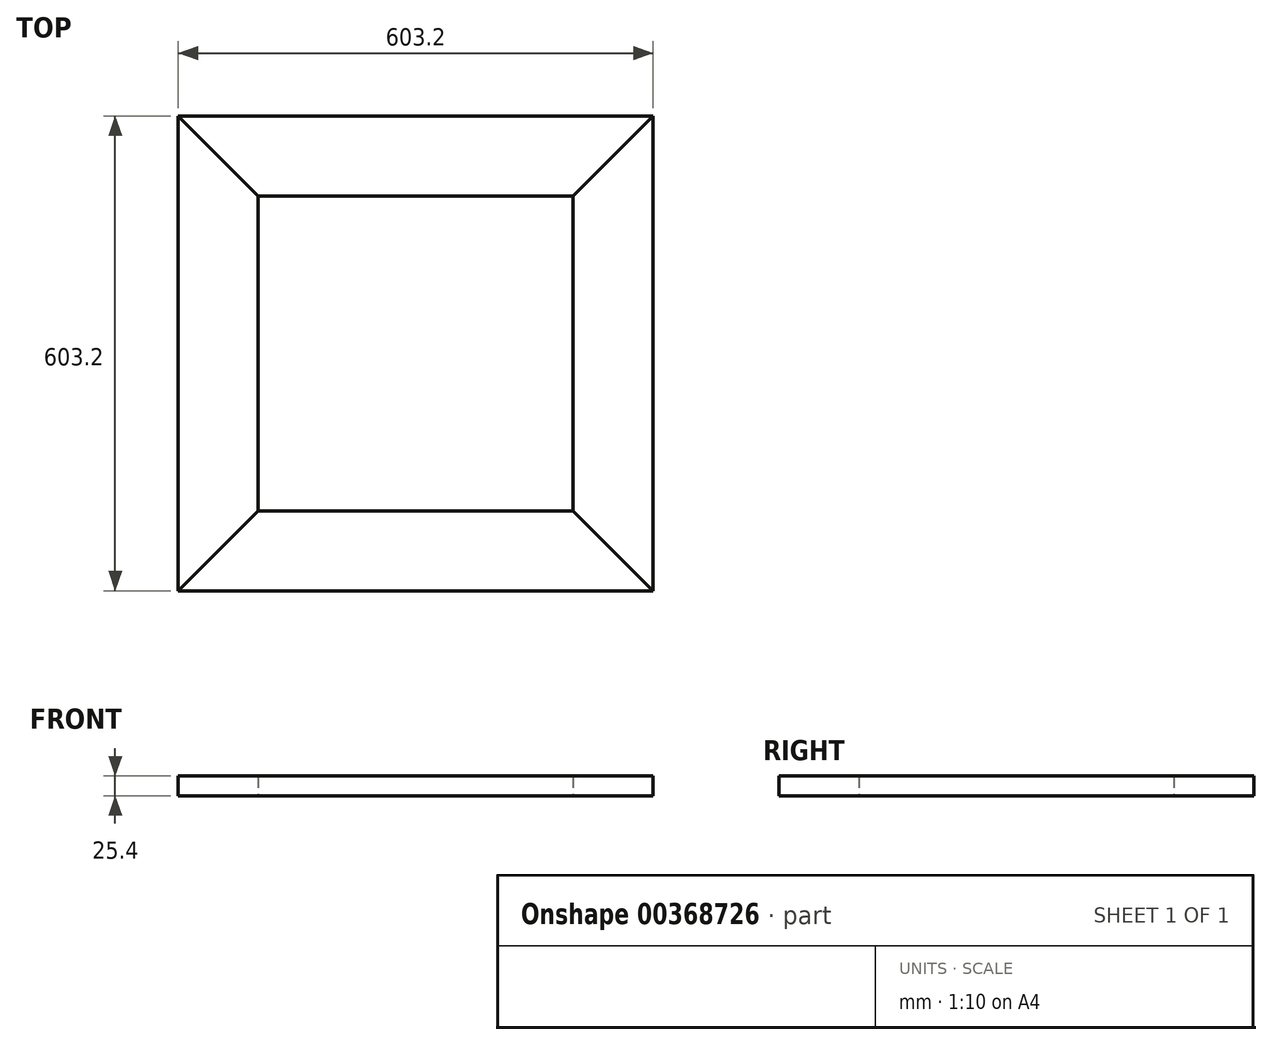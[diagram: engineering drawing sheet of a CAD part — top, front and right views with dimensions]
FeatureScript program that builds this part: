
annotation { "Feature Type Name" : "Feature", "Feature Type Description" : "" }
export const myFeature = defineFeature(function(context is Context, id is Id, definition is map)
    precondition{}
    {
        {
            var Q0;
            Q0=qCreatedBy(makeId("Top.planeOp"),FACE);
            var sketch = newSketch(context, id + "F0", { "sketchPlane" : qUnion([Q0])});
            skLineSegment(sketch, "E0.bottom", {"start": v(200, 200) * mm, "end": v(-200, 200) * mm});
            skLineSegment(sketch, "E0.top", {"start": v(200, -200) * mm, "end": v(-200, -200) * mm});
            skLineSegment(sketch, "E0.left", {"start": v(200, 200) * mm, "end": v(200, -200) * mm});
            skLineSegment(sketch, "E0.right", {"start": v(-200, 200) * mm, "end": v(-200, -200) * mm});
            skPoint(sketch, "E0.middle", {"position": v(0, 0) * mm});
            skLineSegment(sketch, "E1.bottom", {"start": v(301.6, 301.6) * mm, "end": v(-301.6, 301.6) * mm});
            skLineSegment(sketch, "E1.top", {"start": v(301.6, -301.6) * mm, "end": v(-301.6, -301.6) * mm});
            skLineSegment(sketch, "E1.left", {"start": v(301.6, 301.6) * mm, "end": v(301.6, -301.6) * mm});
            skLineSegment(sketch, "E1.right", {"start": v(-301.6, 301.6) * mm, "end": v(-301.6, -301.6) * mm});
            skLineSegment(sketch, "E2", {"start": v(-301.6, 301.6) * mm, "end": v(-200, 200) * mm});
            skLineSegment(sketch, "E3", {"start": v(200, 200) * mm, "end": v(301.6, 301.6) * mm});
            skLineSegment(sketch, "E4", {"start": v(301.6, -301.6) * mm, "end": v(200, -200) * mm});
            skLineSegment(sketch, "E5", {"start": v(-301.6, -301.6) * mm, "end": v(-200, -200) * mm});
            skSolve(sketch);
        }
        {
            var Q0;
            Q0=makeQuery(id+"F0.imprint","IMPRINT",FACE,{"disambiguationData":[TD([[makeQuery(id+"F0.imprint","IMPRINT",EDGE,{"derivedFrom":sQuery(id+"F0.wireOp",EDGE,"E0.bottom")}),-1.0]])]});
            extrude(context, id + "F1", {"entities" : qUnion([Q0]), "depth" : 25.4 * mm, "offsetDistance" : 25.4 * mm});
        }
        {
            var Q0;
            Q0=makeQuery(id+"F0.imprint","IMPRINT",FACE,{"disambiguationData":[TD([[makeQuery(id+"F0.imprint","IMPRINT",EDGE,{"derivedFrom":sQuery(id+"F0.wireOp",EDGE,"E0.right")}),-1.0]])]});
            extrude(context, id + "F2", {"entities" : qUnion([Q0]), "depth" : 25.4 * mm, "offsetDistance" : 25.4 * mm});
        }
        {
            var Q0;
            Q0=makeQuery(id+"F0.imprint","IMPRINT",FACE,{"disambiguationData":[TD([[makeQuery(id+"F0.imprint","IMPRINT",EDGE,{"derivedFrom":sQuery(id+"F0.wireOp",EDGE,"E0.top")}),1.0]])]});
            extrude(context, id + "F3", {"entities" : qUnion([Q0]), "depth" : 25.4 * mm, "offsetDistance" : 25.4 * mm});
        }
        {
            var Q0;
            Q0=makeQuery(id+"F0.imprint","IMPRINT",FACE,{"disambiguationData":[TD([[makeQuery(id+"F0.imprint","IMPRINT",EDGE,{"derivedFrom":sQuery(id+"F0.wireOp",EDGE,"E0.left")}),1.0]])]});
            extrude(context, id + "F4", {"entities" : qUnion([Q0]), "depth" : 25.4 * mm, "offsetDistance" : 25.4 * mm});
        }
    });
